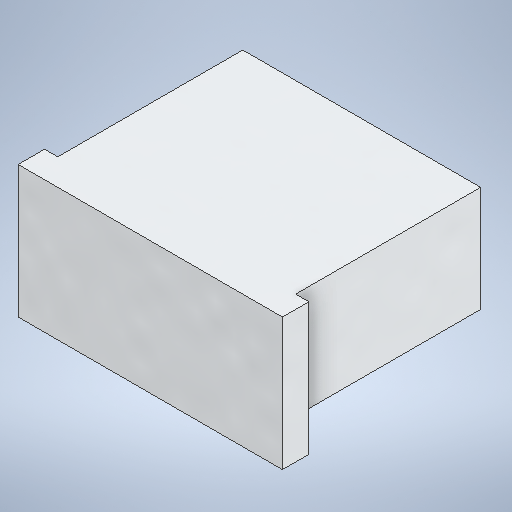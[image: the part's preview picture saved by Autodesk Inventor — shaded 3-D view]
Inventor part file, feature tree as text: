
AUTODESK INVENTOR PART (.ipt)
format: ipt  version: 2025.1 (Build 291241020, 241B)  size: 241,152 bytes
history: native  units: mm
features: extrude x3, sketch x3
ambient origin geometry x8: Origin, YZ Plane, XZ Plane, XY Plane, X Axis, Y Axis, Z Axis, Center Point
bodies: Solid1 (feature_tree)
feature tree (6):
  extrude  "Extrusion1"  Depth=4.0mm
  extrude  "Extrusion2"  Depth=10.0mm
  extrude  "Extrusion3"  Depth=1.0mm TaperAngle=0.0deg
  sketch  "Sketch1"  dims[d0=9.0mm d1=4.0mm]
  sketch  "Sketch2"  dims[d2=7.0mm d3=0.0mm d4=10.0mm]
  sketch  "Sketch3"  dims[d5=5.0mm d6=1.0mm d7=0.0mm d8=0.8mm d9=0.8mm d10=6.5mm d11=0.0mm]
